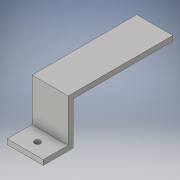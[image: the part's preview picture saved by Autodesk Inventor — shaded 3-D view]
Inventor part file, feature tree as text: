
AUTODESK INVENTOR PART (.ipt)
format: ipt  version: 2016 (Build 200138000, 138)  size: 105,984 bytes
history: native  units: in
note: dims shown in document units (in); Inventor stores cm internally (conversion verified against a paired STEP export)
features: extrude x2, sketch x2
ambient origin geometry x8: Origin, YZ Plane, XZ Plane, XY Plane, X Axis, Y Axis, Z Axis, Center Point
bodies: Solid1 (feature_tree)
feature tree (4):
  extrude  "Extrusion1"  Depth=0.5in
  extrude  "Extrusion2"  Depth=0.1in
  sketch  "Sketch1"  dims[d0=0.5in d1=0.5in]
  sketch  "Sketch2"  dims[d2=0.1in d3=0.1in d4=2.0in d5=0.1in d6=0.725in d7=0.0in d8=0.1181in d9=0.725in d10=0.0in]
